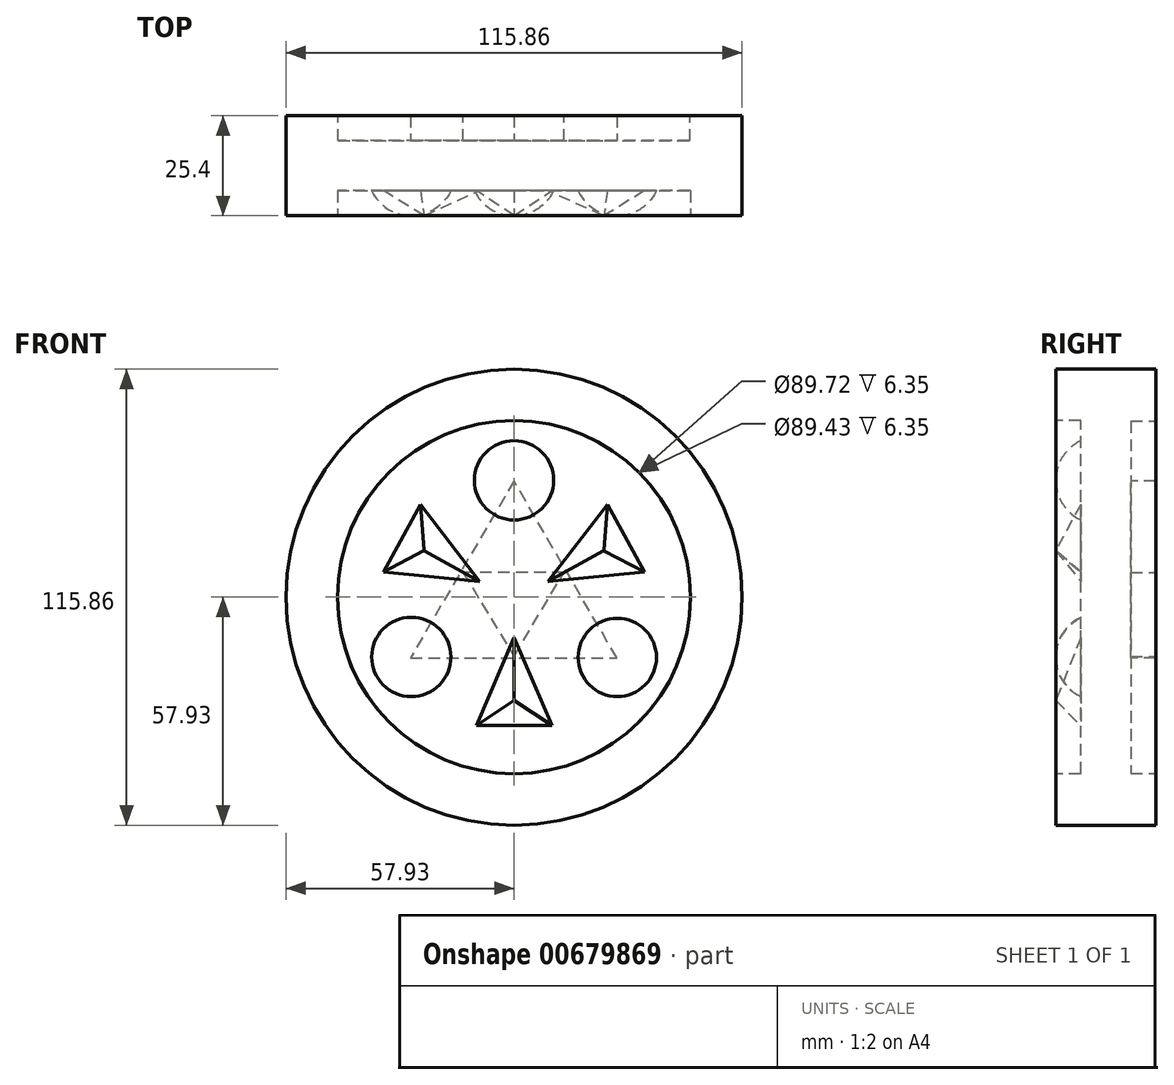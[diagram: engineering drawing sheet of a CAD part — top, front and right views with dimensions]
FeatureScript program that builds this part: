
annotation { "Feature Type Name" : "Feature", "Feature Type Description" : "" }
export const myFeature = defineFeature(function(context is Context, id is Id, definition is map)
    precondition{}
    {
        {
            var Q0;
            Q0=qCreatedBy(makeId("Front.planeOp"),FACE);
            var sketch = newSketch(context, id + "F0", { "sketchPlane" : qUnion([Q0])});
            skCircle(sketch, "E0", {"center": v(0, 0) * mm, "radius": 57.93 * mm});
            skCircle(sketch, "E1", {"center": v(0, 0) * mm, "radius": 45.24 * mm});
            skLineSegment(sketch, "E2", {"start": v(-24.01, 26.9) * mm, "end": v(-4.53, 1.77) * mm});
            skLineSegment(sketch, "E3", {"start": v(-4.53, 1.77) * mm, "end": v(-36.03, 4.88) * mm});
            skLineSegment(sketch, "E4", {"start": v(-36.03, 4.88) * mm, "end": v(-24.01, 26.9) * mm});
            skCircle(sketch, "E5", {"center": v(0, 29.6) * mm, "radius": 10.34 * mm});
            skLineSegment(sketch, "E6", {"start": v(4.46, 1.76) * mm, "end": v(24, 26.88) * mm});
            skLineSegment(sketch, "E7", {"start": v(24, 26.88) * mm, "end": v(36.16, 4.84) * mm});
            skLineSegment(sketch, "E8", {"start": v(36.16, 4.84) * mm, "end": v(4.46, 1.76) * mm});
            skLineSegment(sketch, "E9", {"start": v(0, -5.39) * mm, "end": v(12.64, -34.5) * mm});
            skLineSegment(sketch, "E10", {"start": v(12.64, -34.5) * mm, "end": v(-12.54, -34.5) * mm});
            skLineSegment(sketch, "E11", {"start": v(-12.54, -34.5) * mm, "end": v(0, -5.39) * mm});
            skCircle(sketch, "E12", {"center": v(-26.13, -15.37) * mm, "radius": 10.23 * mm});
            skCircle(sketch, "E13", {"center": v(26.13, -15.19) * mm, "radius": 9.93 * mm});
            skSolve(sketch);
        }
        {
            var Q0;
            Q0=makeQuery(id+"F0.imprint","IMPRINT",FACE,{"disambiguationData":[TD([[makeQuery(id+"F0.imprint","IMPRINT",EDGE,{"derivedFrom":sQuery(id+"F0.wireOp",EDGE,"E0")}),1.0]])]});
            var Q1;
            Q1=makeQuery(id+"F0.imprint","IMPRINT",FACE,{"disambiguationData":[TD([[makeQuery(id+"F0.imprint","IMPRINT",EDGE,{"derivedFrom":sQuery(id+"F0.wireOp",EDGE,"E1")}),1.0]])]});
            var Q2;
            Q2=makeQuery(id+"F0.imprint","IMPRINT",FACE,{"disambiguationData":[TD([[makeQuery(id+"F0.imprint","IMPRINT",EDGE,{"derivedFrom":sQuery(id+"F0.wireOp",EDGE,"E5")}),1.0]])]});
            var Q3;
            Q3=makeQuery(id+"F0.imprint","IMPRINT",FACE,{"disambiguationData":[TD([[makeQuery(id+"F0.imprint","IMPRINT",EDGE,{"derivedFrom":sQuery(id+"F0.wireOp",EDGE,"E2")}),-1.0]])]});
            var Q4;
            Q4=makeQuery(id+"F0.imprint","IMPRINT",FACE,{"disambiguationData":[TD([[makeQuery(id+"F0.imprint","IMPRINT",EDGE,{"derivedFrom":sQuery(id+"F0.wireOp",EDGE,"E12")}),1.0]])]});
            var Q5;
            Q5=makeQuery(id+"F0.imprint","IMPRINT",FACE,{"disambiguationData":[TD([[makeQuery(id+"F0.imprint","IMPRINT",EDGE,{"derivedFrom":sQuery(id+"F0.wireOp",EDGE,"E9")}),-1.0]])]});
            var Q6;
            Q6=makeQuery(id+"F0.imprint","IMPRINT",FACE,{"disambiguationData":[TD([[makeQuery(id+"F0.imprint","IMPRINT",EDGE,{"derivedFrom":sQuery(id+"F0.wireOp",EDGE,"E13")}),1.0]])]});
            var Q7;
            Q7=makeQuery(id+"F0.imprint","IMPRINT",FACE,{"disambiguationData":[TD([[makeQuery(id+"F0.imprint","IMPRINT",EDGE,{"derivedFrom":sQuery(id+"F0.wireOp",EDGE,"E6")}),-1.0]])]});
            extrude(context, id + "F1", {"entities" : qUnion([Q0, Q1, Q2, Q3, Q4, Q5, Q6, Q7]), "depth" : 12.7 * mm, "offsetDistance" : 25.4 * mm});
        }
        {
            var Q0;
            Q0=makeQuery(id+"F1.opExtrude","CAP_FACE",FACE,{"disambiguationData":[OSD([sQuery(id+"F0.wireOp",EDGE,"E0")])],"isStart":true});
            extrude(context, id + "F2", {"entities" : qUnion([Q0]), "operationType" : NewBodyOperationType.ADD, "depth" : 12.7 * mm, "offsetDistance" : 25.4 * mm});
        }
        {
            var Q0;
            Q0=makeQuery(id+"F1.opExtrude","CAP_FACE",FACE,{"disambiguationData":[OSD([sQuery(id+"F0.wireOp",EDGE,"E0")])],"isStart":false});
            var sketch = newSketch(context, id + "F3", { "sketchPlane" : qUnion([Q0])});
            skCircle(sketch, "E14", {"center": v(0, 0) * mm, "radius": 44.86 * mm});
            skSolve(sketch);
        }
        {
            var Q0;
            Q0=makeQuery(id+"F3.imprint","IMPRINT",FACE,{"disambiguationData":[TD([[makeQuery(id+"F3.imprint","IMPRINT",EDGE,{"derivedFrom":sQuery(id+"F3.wireOp",EDGE,"E14")}),1.0]])]});
            extrude(context, id + "F4", {"entities" : qUnion([Q0]), "operationType" : NewBodyOperationType.REMOVE, "oppositeDirection" : true, "depth" : 6.35 * mm, "offsetDistance" : 25.4 * mm});
        }
        {
            var Q0;
            Q0=makeQuery(id+"F2.opExtrude","CAP_FACE",FACE,{"disambiguationData":[OSD([sQuery(id+"F0.wireOp",EDGE,"E0")])],"isStart":false});
            var sketch = newSketch(context, id + "F5", { "sketchPlane" : qUnion([Q0])});
            skCircle(sketch, "E15", {"center": v(0, 0) * mm, "radius": 44.72 * mm});
            skSolve(sketch);
        }
        {
            var Q0;
            Q0=makeQuery(id+"F5.imprint","IMPRINT",FACE,{"disambiguationData":[TD([[makeQuery(id+"F5.imprint","IMPRINT",EDGE,{"derivedFrom":sQuery(id+"F5.wireOp",EDGE,"E15")}),1.0]])]});
            extrude(context, id + "F6", {"entities" : qUnion([Q0]), "operationType" : NewBodyOperationType.REMOVE, "oppositeDirection" : true, "depth" : 6.35 * mm, "offsetDistance" : 25.4 * mm});
        }
        {
            var Q0;
            Q0=makeQuery(id+"F4.boolean.opBoolean","COPY",FACE,{"derivedFrom":makeQuery(id+"F4.opExtrude","CAP_FACE",FACE,{"disambiguationData":[OSD([sQuery(id+"F3.wireOp",EDGE,"E14")])],"isStart":false})});
            var sketch = newSketch(context, id + "F7", { "sketchPlane" : qUnion([Q0])});
            skCircle(sketch, "E16", {"center": v(0, 29.7) * mm, "radius": 10.07 * mm});
            skCircle(sketch, "E17", {"center": v(26.24, -15.3) * mm, "radius": 9.95 * mm});
            skCircle(sketch, "E18", {"center": v(-26.1, -15.18) * mm, "radius": 10.08 * mm});
            skSolve(sketch);
        }
        {
            var Q0;
            Q0=makeQuery(id+"F7.imprint","IMPRINT",FACE,{"disambiguationData":[TD([[makeQuery(id+"F7.imprint","IMPRINT",EDGE,{"derivedFrom":sQuery(id+"F7.wireOp",EDGE,"E16")}),1.0]])]});
            var Q1;
            Q1=makeQuery(id+"F7.imprint","IMPRINT",FACE,{"disambiguationData":[TD([[makeQuery(id+"F7.imprint","IMPRINT",EDGE,{"derivedFrom":sQuery(id+"F7.wireOp",EDGE,"E17")}),1.0]])]});
            var Q2;
            Q2=makeQuery(id+"F7.imprint","IMPRINT",FACE,{"disambiguationData":[TD([[makeQuery(id+"F7.imprint","IMPRINT",EDGE,{"derivedFrom":sQuery(id+"F7.wireOp",EDGE,"E18")}),1.0]])]});
            extrude(context, id + "F8", {"entities" : qUnion([Q0, Q1, Q2]), "operationType" : NewBodyOperationType.ADD, "depth" : 6.35 * mm, "offsetDistance" : 25.4 * mm});
        }
        {
            var Q0;
            Q0=makeQuery(id+"F8.opExtrude","CAP_FACE",FACE,{"disambiguationData":[OSD([sQuery(id+"F7.wireOp",EDGE,"E16")])],"isStart":false});
            fillet(context, id + "F9", {"entities" : qUnion([Q0]), "radius" : 11.1 * mm, "tangentPropagation" : true, "allowEdgeOverflow" : false});
        }
        {
            var Q0;
            Q0=makeQuery(id+"F8.opExtrude","CAP_FACE",FACE,{"disambiguationData":[OSD([sQuery(id+"F7.wireOp",EDGE,"E18")])],"isStart":false});
            fillet(context, id + "F10", {"entities" : qUnion([Q0]), "radius" : 11.1 * mm, "tangentPropagation" : true, "allowEdgeOverflow" : false});
        }
        {
            var Q0;
            Q0=makeQuery(id+"F8.opExtrude","CAP_FACE",FACE,{"disambiguationData":[OSD([sQuery(id+"F7.wireOp",EDGE,"E17")])],"isStart":false});
            fillet(context, id + "F11", {"entities" : qUnion([Q0]), "radius" : 10.82 * mm, "tangentPropagation" : true, "allowEdgeOverflow" : false});
        }
        {
            var Q0;
            Q0=makeQuery(id+"F4.boolean.opBoolean","COPY",FACE,{"derivedFrom":makeQuery(id+"F4.opExtrude","CAP_FACE",FACE,{"disambiguationData":[OSD([sQuery(id+"F3.wireOp",EDGE,"E14")])],"isStart":false})});
            var sketch = newSketch(context, id + "F12", { "sketchPlane" : qUnion([Q0])});
            skLineSegment(sketch, "E19", {"start": v(-24.01, 27.05) * mm, "end": v(-4.53, 1.7) * mm});
            skLineSegment(sketch, "E20", {"start": v(-4.53, 1.7) * mm, "end": v(-36.2, 4.79) * mm});
            skLineSegment(sketch, "E21", {"start": v(-36.2, 4.79) * mm, "end": v(-24.01, 27.05) * mm});
            skLineSegment(sketch, "E22", {"start": v(23.98, 27.05) * mm, "end": v(4.4, 1.65) * mm});
            skLineSegment(sketch, "E23", {"start": v(4.4, 1.65) * mm, "end": v(36.2, 4.79) * mm});
            skLineSegment(sketch, "E24", {"start": v(36.2, 4.79) * mm, "end": v(23.98, 27.05) * mm});
            skLineSegment(sketch, "E25", {"start": v(0, -5.35) * mm, "end": v(12.6, -34.53) * mm});
            skLineSegment(sketch, "E26", {"start": v(12.6, -34.53) * mm, "end": v(-12.46, -34.53) * mm});
            skLineSegment(sketch, "E27", {"start": v(-12.46, -34.53) * mm, "end": v(0, -5.35) * mm});
            skSolve(sketch);
        }
        {
            var Q0;
            Q0=makeQuery(id+"F12.imprint","IMPRINT",FACE,{"disambiguationData":[TD([[makeQuery(id+"F12.imprint","IMPRINT",EDGE,{"derivedFrom":sQuery(id+"F12.wireOp",EDGE,"E19")}),-1.0]])]});
            var Q1;
            Q1=makeQuery(id+"F12.imprint","IMPRINT",FACE,{"disambiguationData":[TD([[makeQuery(id+"F12.imprint","IMPRINT",EDGE,{"derivedFrom":sQuery(id+"F12.wireOp",EDGE,"E22")}),1.0]])]});
            var Q2;
            Q2=makeQuery(id+"F12.imprint","IMPRINT",FACE,{"disambiguationData":[TD([[makeQuery(id+"F12.imprint","IMPRINT",EDGE,{"derivedFrom":sQuery(id+"F12.wireOp",EDGE,"E25")}),-1.0]])]});
            extrude(context, id + "F13", {"entities" : qUnion([Q0, Q1, Q2]), "operationType" : NewBodyOperationType.ADD, "depth" : 6.35 * mm, "offsetDistance" : 25.4 * mm});
        }
        {
            var Q0;
            Q0=makeQuery(id+"F13.opExtrude","CAP_FACE",FACE,{"disambiguationData":[OSD([sQuery(id+"F12.wireOp",EDGE,"E19"),sQuery(id+"F12.wireOp",EDGE,"E20"),sQuery(id+"F12.wireOp",EDGE,"E21")])],"isStart":false});
            chamfer(context, id + "F14", {"entities" : qUnion([Q0]), "width" : 8.28 * mm, "tangentPropagation" : true});
        }
        {
            var Q0;
            Q0=makeQuery(id+"F13.opExtrude","CAP_FACE",FACE,{"disambiguationData":[OSD([sQuery(id+"F12.wireOp",EDGE,"E22"),sQuery(id+"F12.wireOp",EDGE,"E23"),sQuery(id+"F12.wireOp",EDGE,"E24")])],"isStart":false});
            chamfer(context, id + "F15", {"entities" : qUnion([Q0]), "width" : 8.28 * mm, "tangentPropagation" : true});
        }
        {
            var Q0;
            Q0=makeQuery(id+"F13.opExtrude","CAP_FACE",FACE,{"disambiguationData":[OSD([sQuery(id+"F12.wireOp",EDGE,"E25"),sQuery(id+"F12.wireOp",EDGE,"E26"),sQuery(id+"F12.wireOp",EDGE,"E27")])],"isStart":false});
            chamfer(context, id + "F16", {"entities" : qUnion([Q0]), "width" : 8.25 * mm, "tangentPropagation" : true});
        }
        {
            var Q0;
            Q0=makeQuery(id+"F6.boolean.opBoolean","COPY",FACE,{"derivedFrom":makeQuery(id+"F6.opExtrude","CAP_FACE",FACE,{"disambiguationData":[OSD([sQuery(id+"F5.wireOp",EDGE,"E15")])],"isStart":false})});
            var sketch = newSketch(context, id + "F17", { "sketchPlane" : qUnion([Q0])});
            skLineSegment(sketch, "E28", {"start": v(0, 29.52) * mm, "end": v(26.34, -15.44) * mm});
            skLineSegment(sketch, "E29", {"start": v(26.34, -15.44) * mm, "end": v(-26.11, -15.44) * mm});
            skLineSegment(sketch, "E30", {"start": v(-26.11, -15.44) * mm, "end": v(0, 29.52) * mm});
            skLineSegment(sketch, "E31", {"start": v(13.17, 7.04) * mm, "end": v(0.11, -15.44) * mm});
            skLineSegment(sketch, "E32", {"start": v(0.11, -15.44) * mm, "end": v(-13.06, 7.04) * mm});
            skLineSegment(sketch, "E33", {"start": v(-13.06, 7.04) * mm, "end": v(13.17, 7.04) * mm});
            skSolve(sketch);
        }
        {
            var Q0;
            {var subQ3=sQuery(id+"F17.wireOp",EDGE,"E32");Q0=makeQuery(id+"F17.imprint","IMPRINT",FACE,{"disambiguationData":[TD([[makeQuery(id+"F17.imprint","IMPRINT",EDGE,{"derivedFrom":subQ3}),1.0]])]});}
            var Q1;
            Q1=makeQuery(id+"F17.imprint","IMPRINT",FACE,{"disambiguationData":[TD([[makeQuery(id+"F17.imprint","IMPRINT",EDGE,{"derivedFrom":sQuery(id+"F17.wireOp",EDGE,"E31")}),-1.0]])]});
            var Q2;
            {var subQ3=sQuery(id+"F17.wireOp",EDGE,"E33");Q2=makeQuery(id+"F17.imprint","IMPRINT",FACE,{"disambiguationData":[TD([[makeQuery(id+"F17.imprint","IMPRINT",EDGE,{"derivedFrom":subQ3}),1.0]])]});}
            var Q3;
            {var subQ3=sQuery(id+"F17.wireOp",EDGE,"E31");Q3=makeQuery(id+"F17.imprint","IMPRINT",FACE,{"disambiguationData":[TD([[makeQuery(id+"F17.imprint","IMPRINT",EDGE,{"derivedFrom":subQ3}),1.0]])]});}
            extrude(context, id + "F18", {"entities" : qUnion([Q0, Q1, Q2, Q3]), "operationType" : NewBodyOperationType.ADD, "depth" : 6.35 * mm, "offsetDistance" : 25.4 * mm});
        }
        {
            var Q0;
            Q0=makeQuery(id+"F18.opExtrude","CAP_FACE",FACE,{"disambiguationData":[OSD([sQuery(id+"F17.wireOp",EDGE,"E28"),sQuery(id+"F17.wireOp",EDGE,"E29"),sQuery(id+"F17.wireOp",EDGE,"E30")])],"isStart":false});
            var sketch = newSketch(context, id + "F19", { "sketchPlane" : qUnion([Q0])});
            skLineSegment(sketch, "E34", {"start": v(-12.72, 6.35) * mm, "end": v(12.98, 6.35) * mm});
            skLineSegment(sketch, "E35", {"start": v(12.98, 6.35) * mm, "end": v(0, -15) * mm});
            skLineSegment(sketch, "E36", {"start": v(0, -15) * mm, "end": v(-12.72, 6.35) * mm});
            skSolve(sketch);
        }
        {
            var Q0;
            Q0=makeQuery(id+"F19.imprint","IMPRINT",FACE,{"disambiguationData":[TD([[makeQuery(id+"F19.imprint","IMPRINT",EDGE,{"derivedFrom":sQuery(id+"F19.wireOp",EDGE,"E34")}),-1.0]])]});
            extrude(context, id + "F20", {"entities" : qUnion([Q0]), "operationType" : NewBodyOperationType.REMOVE, "oppositeDirection" : true, "depth" : 6.35 * mm, "offsetDistance" : 25.4 * mm});
        }
    });
